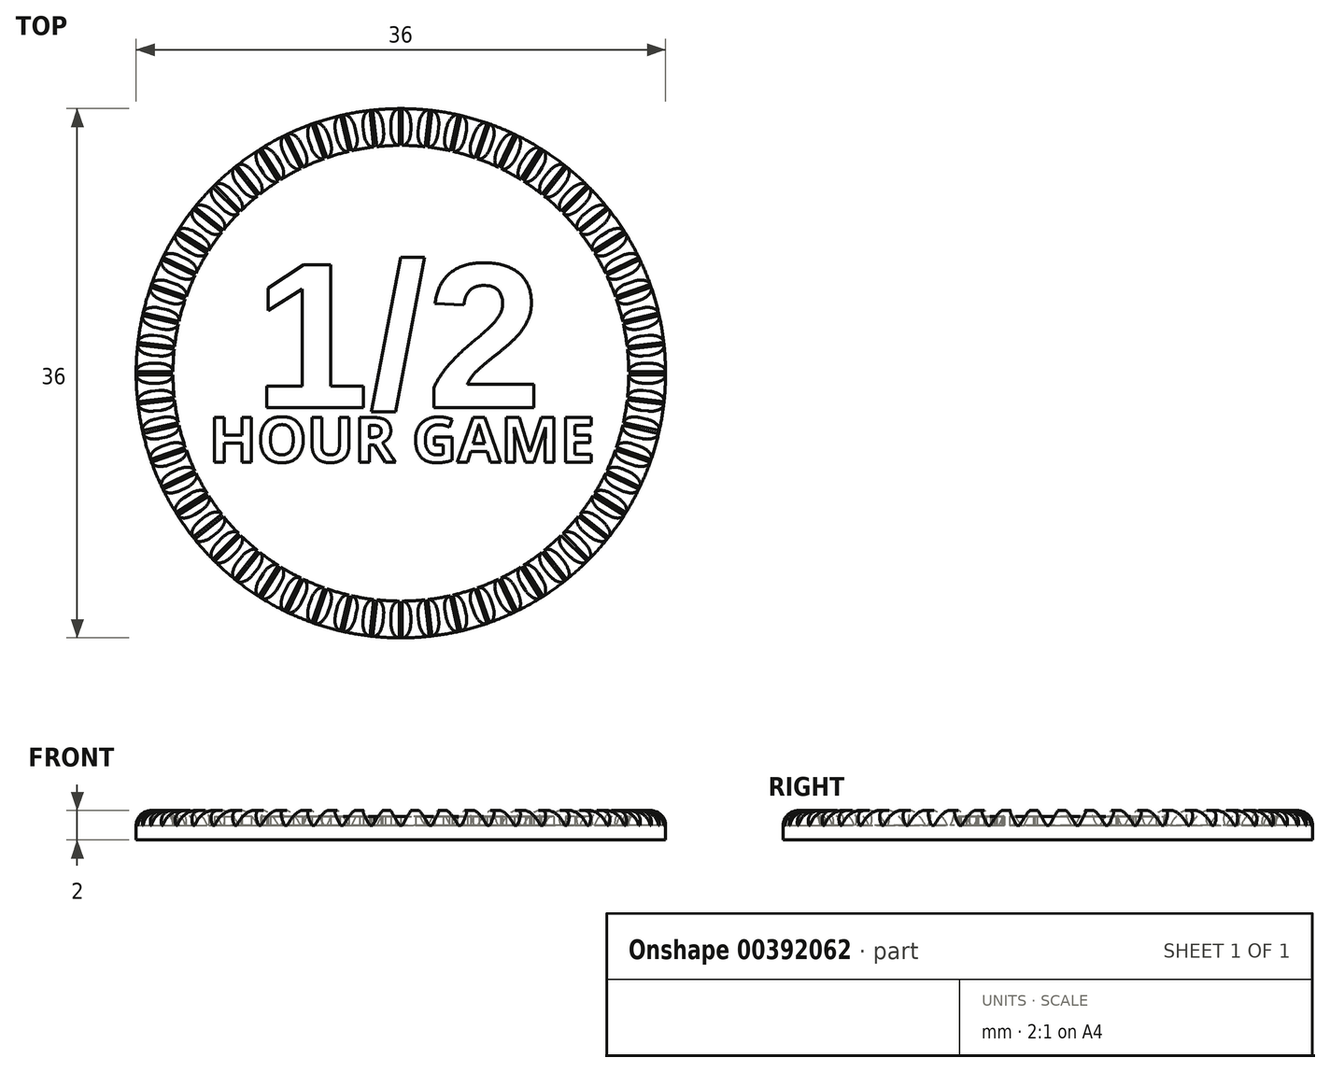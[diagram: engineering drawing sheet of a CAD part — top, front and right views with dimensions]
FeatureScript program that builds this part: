
annotation { "Feature Type Name" : "Feature", "Feature Type Description" : "" }
export const myFeature = defineFeature(function(context is Context, id is Id, definition is map)
    precondition{}
    {
        {
            var Q0;
            Q0=qCreatedBy(makeId("Top.planeOp"),FACE);
            var sketch = newSketch(context, id + "F0", { "sketchPlane" : qUnion([Q0])});
            skCircle(sketch, "E0", {"center": v(0, 0) * mm, "radius": 18 * mm});
            skSolve(sketch);
        }
        {
            var Q0;
            Q0=qSketchRegion(id+"F0",true);
            extrude(context, id + "F1", {"entities" : qUnion([Q0]), "depth" : 2 * mm});
        }
        {
            var Q0;
            Q0=makeQuery(id+"F1.opExtrude","CAP_FACE",FACE,{"disambiguationData":[OSD([sQuery(id+"F0.wireOp",EDGE,"E0")])],"isStart":false});
            var sketch = newSketch(context, id + "F2", { "sketchPlane" : qUnion([Q0])});
            skCircle(sketch, "E1.0", {"center": v(0, 0) * mm, "radius": 15.5 * mm});
            skSolve(sketch);
        }
        {
            var Q0;
            Q0=qSketchRegion(id+"F2",true);
            extrude(context, id + "F3", {"entities" : qUnion([Q0]), "operationType" : NewBodyOperationType.REMOVE, "oppositeDirection" : true, "depth" : 1 * mm});
        }
        {
            var Q0;
            Q0=makeQuery(id+"F1.opExtrude","CAP_FACE",FACE,{"disambiguationData":[OSD([sQuery(id+"F0.wireOp",EDGE,"E0")])],"isStart":false});
            fillet(context, id + "F4", {"entities" : qUnion([Q0]), "radius" : 1 * mm, "tangentPropagation" : true, "allowEdgeOverflow" : false});
        }
        {
            var Q0;
            Q0=qCreatedBy(makeId("Right.planeOp"),FACE);
            var sketch = newSketch(context, id + "F5", { "sketchPlane" : qUnion([Q0])});
            skLineSegment(sketch, "E2", {"start": v(0, 0) * mm, "end": v(0, 4.13) * mm, "construction": true});
            skLineSegment(sketch, "E3", {"start": v(0, 1) * mm, "end": v(-0.1, 1) * mm});
            skLineSegment(sketch, "E4", {"start": v(-0.1, 1) * mm, "end": v(-0.68, 2) * mm});
            skLineSegment(sketch, "E5", {"start": v(-0.68, 2) * mm, "end": v(0, 2) * mm});
            skLineSegment(sketch, "E6.MirrorCS", {"start": v(0, 1) * mm, "end": v(0.1, 1) * mm});
            skLineSegment(sketch, "E7.MirrorCS", {"start": v(0.68, 2) * mm, "end": v(0, 2) * mm});
            skLineSegment(sketch, "E8.MirrorCS", {"start": v(0.1, 1) * mm, "end": v(0.68, 2) * mm});
            skSolve(sketch);
        }
        {
            var Q0;
            Q0=qSketchRegion(id+"F5",true);
            extrude(context, id + "F6", {"entities" : qUnion([Q0]), "endBound" : BoundingType.THROUGH_ALL, "oppositeDirection" : true, "depth" : 25 * mm});
        }
        {
            var Q0;
            Q0=qCreatedBy(makeId("Front.planeOp"),FACE);
            var sketch = newSketch(context, id + "F7", { "sketchPlane" : qUnion([Q0])});
            skLineSegment(sketch, "E9", {"start": v(0, 0) * mm, "end": v(0, 9.54) * mm});
            skSolve(sketch);
        }
        {
            var Q0;
            Q0=makeQuery(id+"F6.opExtrude","SWEPT_BODY",BODY,{"disambiguationData":[OSD([sQuery(id+"F5.wireOp",EDGE,"E3"),sQuery(id+"F5.wireOp",EDGE,"E4"),sQuery(id+"F5.wireOp",EDGE,"E5"),sQuery(id+"F5.wireOp",EDGE,"E6.MirrorCS"),sQuery(id+"F5.wireOp",EDGE,"E7.MirrorCS"),sQuery(id+"F5.wireOp",EDGE,"E8.MirrorCS")])]});
            var Q1;
            Q1=sQuery(id+"F7.wireOp",EDGE,"E9");
            circularPattern(context, id + "F8", {"operationType" : NewBodyOperationType.REMOVE, "entities" : qUnion([Q0]), "axis" : qUnion([Q1]), "angle" : 360 * degree, "instanceCount" : 56, "equalSpace" : true, "computeTransformsWithoutBuiltin" : true});
        }
        {
            var Q0;
            {var subQ0=makeQuery(id+"F6.opExtrude","SWEPT_FACE",FACE,{"disambiguationData":[OSD([sQuery(id+"F5.wireOp",EDGE,"E3"),sQuery(id+"F5.wireOp",EDGE,"E6.MirrorCS")])]});Q0=makeQuery(id+"F8.boolean.opBoolean","MERGE",FACE,{"derivedFrom":[makeQuery(id+"F3.boolean.opBoolean","COPY",FACE,{"derivedFrom":makeQuery(id+"F3.opExtrude","CAP_FACE",FACE,{"disambiguationData":[OSD([sQuery(id+"F2.wireOp",EDGE,"E1.0")])],"isStart":false})}),subQ0,makeQuery(id+"F8.opPattern","COPY",FACE,{"derivedFrom":subQ0,"instanceName":"1"}),makeQuery(id+"F8.opPattern","COPY",FACE,{"derivedFrom":subQ0,"instanceName":"2"}),makeQuery(id+"F8.opPattern","COPY",FACE,{"derivedFrom":subQ0,"instanceName":"3"}),makeQuery(id+"F8.opPattern","COPY",FACE,{"derivedFrom":subQ0,"instanceName":"4"}),makeQuery(id+"F8.opPattern","COPY",FACE,{"derivedFrom":subQ0,"instanceName":"5"}),makeQuery(id+"F8.opPattern","COPY",FACE,{"derivedFrom":subQ0,"instanceName":"6"}),makeQuery(id+"F8.opPattern","COPY",FACE,{"derivedFrom":subQ0,"instanceName":"7"}),makeQuery(id+"F8.opPattern","COPY",FACE,{"derivedFrom":subQ0,"instanceName":"8"}),makeQuery(id+"F8.opPattern","COPY",FACE,{"derivedFrom":subQ0,"instanceName":"9"}),makeQuery(id+"F8.opPattern","COPY",FACE,{"derivedFrom":subQ0,"instanceName":"10"}),makeQuery(id+"F8.opPattern","COPY",FACE,{"derivedFrom":subQ0,"instanceName":"11"}),makeQuery(id+"F8.opPattern","COPY",FACE,{"derivedFrom":subQ0,"instanceName":"12"}),makeQuery(id+"F8.opPattern","COPY",FACE,{"derivedFrom":subQ0,"instanceName":"13"}),makeQuery(id+"F8.opPattern","COPY",FACE,{"derivedFrom":subQ0,"instanceName":"14"}),makeQuery(id+"F8.opPattern","COPY",FACE,{"derivedFrom":subQ0,"instanceName":"15"}),makeQuery(id+"F8.opPattern","COPY",FACE,{"derivedFrom":subQ0,"instanceName":"16"}),makeQuery(id+"F8.opPattern","COPY",FACE,{"derivedFrom":subQ0,"instanceName":"17"}),makeQuery(id+"F8.opPattern","COPY",FACE,{"derivedFrom":subQ0,"instanceName":"18"}),makeQuery(id+"F8.opPattern","COPY",FACE,{"derivedFrom":subQ0,"instanceName":"19"}),makeQuery(id+"F8.opPattern","COPY",FACE,{"derivedFrom":subQ0,"instanceName":"20"}),makeQuery(id+"F8.opPattern","COPY",FACE,{"derivedFrom":subQ0,"instanceName":"21"}),makeQuery(id+"F8.opPattern","COPY",FACE,{"derivedFrom":subQ0,"instanceName":"22"}),makeQuery(id+"F8.opPattern","COPY",FACE,{"derivedFrom":subQ0,"instanceName":"23"}),makeQuery(id+"F8.opPattern","COPY",FACE,{"derivedFrom":subQ0,"instanceName":"24"}),makeQuery(id+"F8.opPattern","COPY",FACE,{"derivedFrom":subQ0,"instanceName":"25"}),makeQuery(id+"F8.opPattern","COPY",FACE,{"derivedFrom":subQ0,"instanceName":"26"}),makeQuery(id+"F8.opPattern","COPY",FACE,{"derivedFrom":subQ0,"instanceName":"27"}),makeQuery(id+"F8.opPattern","COPY",FACE,{"derivedFrom":subQ0,"instanceName":"28"}),makeQuery(id+"F8.opPattern","COPY",FACE,{"derivedFrom":subQ0,"instanceName":"29"}),makeQuery(id+"F8.opPattern","COPY",FACE,{"derivedFrom":subQ0,"instanceName":"30"}),makeQuery(id+"F8.opPattern","COPY",FACE,{"derivedFrom":subQ0,"instanceName":"31"}),makeQuery(id+"F8.opPattern","COPY",FACE,{"derivedFrom":subQ0,"instanceName":"32"}),makeQuery(id+"F8.opPattern","COPY",FACE,{"derivedFrom":subQ0,"instanceName":"33"}),makeQuery(id+"F8.opPattern","COPY",FACE,{"derivedFrom":subQ0,"instanceName":"34"}),makeQuery(id+"F8.opPattern","COPY",FACE,{"derivedFrom":subQ0,"instanceName":"35"}),makeQuery(id+"F8.opPattern","COPY",FACE,{"derivedFrom":subQ0,"instanceName":"36"}),makeQuery(id+"F8.opPattern","COPY",FACE,{"derivedFrom":subQ0,"instanceName":"37"}),makeQuery(id+"F8.opPattern","COPY",FACE,{"derivedFrom":subQ0,"instanceName":"38"}),makeQuery(id+"F8.opPattern","COPY",FACE,{"derivedFrom":subQ0,"instanceName":"39"}),makeQuery(id+"F8.opPattern","COPY",FACE,{"derivedFrom":subQ0,"instanceName":"40"}),makeQuery(id+"F8.opPattern","COPY",FACE,{"derivedFrom":subQ0,"instanceName":"41"}),makeQuery(id+"F8.opPattern","COPY",FACE,{"derivedFrom":subQ0,"instanceName":"42"}),makeQuery(id+"F8.opPattern","COPY",FACE,{"derivedFrom":subQ0,"instanceName":"43"}),makeQuery(id+"F8.opPattern","COPY",FACE,{"derivedFrom":subQ0,"instanceName":"44"}),makeQuery(id+"F8.opPattern","COPY",FACE,{"derivedFrom":subQ0,"instanceName":"45"}),makeQuery(id+"F8.opPattern","COPY",FACE,{"derivedFrom":subQ0,"instanceName":"46"}),makeQuery(id+"F8.opPattern","COPY",FACE,{"derivedFrom":subQ0,"instanceName":"47"}),makeQuery(id+"F8.opPattern","COPY",FACE,{"derivedFrom":subQ0,"instanceName":"48"}),makeQuery(id+"F8.opPattern","COPY",FACE,{"derivedFrom":subQ0,"instanceName":"49"}),makeQuery(id+"F8.opPattern","COPY",FACE,{"derivedFrom":subQ0,"instanceName":"50"}),makeQuery(id+"F8.opPattern","COPY",FACE,{"derivedFrom":subQ0,"instanceName":"51"}),makeQuery(id+"F8.opPattern","COPY",FACE,{"derivedFrom":subQ0,"instanceName":"52"}),makeQuery(id+"F8.opPattern","COPY",FACE,{"derivedFrom":subQ0,"instanceName":"53"}),makeQuery(id+"F8.opPattern","COPY",FACE,{"derivedFrom":subQ0,"instanceName":"54"}),makeQuery(id+"F8.opPattern","COPY",FACE,{"derivedFrom":subQ0,"instanceName":"55"})]});}
            var sketch = newSketch(context, id + "F9", { "sketchPlane" : qUnion([Q0])});
            skText(sketch, "E10", { "text": "1/2", "fontName": "Arimo-Bold.ttf"});
            const initialGuessF9  = {"E10": [-0.01, -0.00233, 1, 0, 0.01015]};
            skSetInitialGuess(sketch, initialGuessF9);
            skSolve(sketch);
        }
        {
            var Q0;
            Q0=qSketchRegion(id+"F9",true);
            extrude(context, id + "F10", {"entities" : qUnion([Q0]), "operationType" : NewBodyOperationType.ADD, "depth" : 0.6 * mm});
        }
        {
            var Q0;
            {var subQ0=makeQuery(id+"F6.opExtrude","SWEPT_FACE",FACE,{"disambiguationData":[OSD([sQuery(id+"F5.wireOp",EDGE,"E3"),sQuery(id+"F5.wireOp",EDGE,"E6.MirrorCS")])]});Q0=makeQuery(id+"F8.boolean.opBoolean","MERGE",FACE,{"derivedFrom":[makeQuery(id+"F3.boolean.opBoolean","COPY",FACE,{"derivedFrom":makeQuery(id+"F3.opExtrude","CAP_FACE",FACE,{"disambiguationData":[OSD([sQuery(id+"F2.wireOp",EDGE,"E1.0")])],"isStart":false})}),subQ0,makeQuery(id+"F8.opPattern","COPY",FACE,{"derivedFrom":subQ0,"instanceName":"1"}),makeQuery(id+"F8.opPattern","COPY",FACE,{"derivedFrom":subQ0,"instanceName":"2"}),makeQuery(id+"F8.opPattern","COPY",FACE,{"derivedFrom":subQ0,"instanceName":"3"}),makeQuery(id+"F8.opPattern","COPY",FACE,{"derivedFrom":subQ0,"instanceName":"4"}),makeQuery(id+"F8.opPattern","COPY",FACE,{"derivedFrom":subQ0,"instanceName":"5"}),makeQuery(id+"F8.opPattern","COPY",FACE,{"derivedFrom":subQ0,"instanceName":"6"}),makeQuery(id+"F8.opPattern","COPY",FACE,{"derivedFrom":subQ0,"instanceName":"7"}),makeQuery(id+"F8.opPattern","COPY",FACE,{"derivedFrom":subQ0,"instanceName":"8"}),makeQuery(id+"F8.opPattern","COPY",FACE,{"derivedFrom":subQ0,"instanceName":"9"}),makeQuery(id+"F8.opPattern","COPY",FACE,{"derivedFrom":subQ0,"instanceName":"10"}),makeQuery(id+"F8.opPattern","COPY",FACE,{"derivedFrom":subQ0,"instanceName":"11"}),makeQuery(id+"F8.opPattern","COPY",FACE,{"derivedFrom":subQ0,"instanceName":"12"}),makeQuery(id+"F8.opPattern","COPY",FACE,{"derivedFrom":subQ0,"instanceName":"13"}),makeQuery(id+"F8.opPattern","COPY",FACE,{"derivedFrom":subQ0,"instanceName":"14"}),makeQuery(id+"F8.opPattern","COPY",FACE,{"derivedFrom":subQ0,"instanceName":"15"}),makeQuery(id+"F8.opPattern","COPY",FACE,{"derivedFrom":subQ0,"instanceName":"16"}),makeQuery(id+"F8.opPattern","COPY",FACE,{"derivedFrom":subQ0,"instanceName":"17"}),makeQuery(id+"F8.opPattern","COPY",FACE,{"derivedFrom":subQ0,"instanceName":"18"}),makeQuery(id+"F8.opPattern","COPY",FACE,{"derivedFrom":subQ0,"instanceName":"19"}),makeQuery(id+"F8.opPattern","COPY",FACE,{"derivedFrom":subQ0,"instanceName":"20"}),makeQuery(id+"F8.opPattern","COPY",FACE,{"derivedFrom":subQ0,"instanceName":"21"}),makeQuery(id+"F8.opPattern","COPY",FACE,{"derivedFrom":subQ0,"instanceName":"22"}),makeQuery(id+"F8.opPattern","COPY",FACE,{"derivedFrom":subQ0,"instanceName":"23"}),makeQuery(id+"F8.opPattern","COPY",FACE,{"derivedFrom":subQ0,"instanceName":"24"}),makeQuery(id+"F8.opPattern","COPY",FACE,{"derivedFrom":subQ0,"instanceName":"25"}),makeQuery(id+"F8.opPattern","COPY",FACE,{"derivedFrom":subQ0,"instanceName":"26"}),makeQuery(id+"F8.opPattern","COPY",FACE,{"derivedFrom":subQ0,"instanceName":"27"}),makeQuery(id+"F8.opPattern","COPY",FACE,{"derivedFrom":subQ0,"instanceName":"28"}),makeQuery(id+"F8.opPattern","COPY",FACE,{"derivedFrom":subQ0,"instanceName":"29"}),makeQuery(id+"F8.opPattern","COPY",FACE,{"derivedFrom":subQ0,"instanceName":"30"}),makeQuery(id+"F8.opPattern","COPY",FACE,{"derivedFrom":subQ0,"instanceName":"31"}),makeQuery(id+"F8.opPattern","COPY",FACE,{"derivedFrom":subQ0,"instanceName":"32"}),makeQuery(id+"F8.opPattern","COPY",FACE,{"derivedFrom":subQ0,"instanceName":"33"}),makeQuery(id+"F8.opPattern","COPY",FACE,{"derivedFrom":subQ0,"instanceName":"34"}),makeQuery(id+"F8.opPattern","COPY",FACE,{"derivedFrom":subQ0,"instanceName":"35"}),makeQuery(id+"F8.opPattern","COPY",FACE,{"derivedFrom":subQ0,"instanceName":"36"}),makeQuery(id+"F8.opPattern","COPY",FACE,{"derivedFrom":subQ0,"instanceName":"37"}),makeQuery(id+"F8.opPattern","COPY",FACE,{"derivedFrom":subQ0,"instanceName":"38"}),makeQuery(id+"F8.opPattern","COPY",FACE,{"derivedFrom":subQ0,"instanceName":"39"}),makeQuery(id+"F8.opPattern","COPY",FACE,{"derivedFrom":subQ0,"instanceName":"40"}),makeQuery(id+"F8.opPattern","COPY",FACE,{"derivedFrom":subQ0,"instanceName":"41"}),makeQuery(id+"F8.opPattern","COPY",FACE,{"derivedFrom":subQ0,"instanceName":"42"}),makeQuery(id+"F8.opPattern","COPY",FACE,{"derivedFrom":subQ0,"instanceName":"43"}),makeQuery(id+"F8.opPattern","COPY",FACE,{"derivedFrom":subQ0,"instanceName":"44"}),makeQuery(id+"F8.opPattern","COPY",FACE,{"derivedFrom":subQ0,"instanceName":"45"}),makeQuery(id+"F8.opPattern","COPY",FACE,{"derivedFrom":subQ0,"instanceName":"46"}),makeQuery(id+"F8.opPattern","COPY",FACE,{"derivedFrom":subQ0,"instanceName":"47"}),makeQuery(id+"F8.opPattern","COPY",FACE,{"derivedFrom":subQ0,"instanceName":"48"}),makeQuery(id+"F8.opPattern","COPY",FACE,{"derivedFrom":subQ0,"instanceName":"49"}),makeQuery(id+"F8.opPattern","COPY",FACE,{"derivedFrom":subQ0,"instanceName":"50"}),makeQuery(id+"F8.opPattern","COPY",FACE,{"derivedFrom":subQ0,"instanceName":"51"}),makeQuery(id+"F8.opPattern","COPY",FACE,{"derivedFrom":subQ0,"instanceName":"52"}),makeQuery(id+"F8.opPattern","COPY",FACE,{"derivedFrom":subQ0,"instanceName":"53"}),makeQuery(id+"F8.opPattern","COPY",FACE,{"derivedFrom":subQ0,"instanceName":"54"}),makeQuery(id+"F8.opPattern","COPY",FACE,{"derivedFrom":subQ0,"instanceName":"55"})]});}
            var sketch = newSketch(context, id + "F11", { "sketchPlane" : qUnion([Q0])});
            skText(sketch, "E11", { "text": "HOUR GAME", "fontName": "OpenSans-Bold.ttf"});
            const initialGuessF11  = {"E11": [-0.01305, -0.00605, 1, 0, 0.00307]};
            skSetInitialGuess(sketch, initialGuessF11);
            skSolve(sketch);
        }
        {
            var Q0;
            Q0=qSketchRegion(id+"F11",true);
            extrude(context, id + "F12", {"entities" : qUnion([Q0]), "operationType" : NewBodyOperationType.ADD, "depth" : 0.6 * mm});
        }
    });
